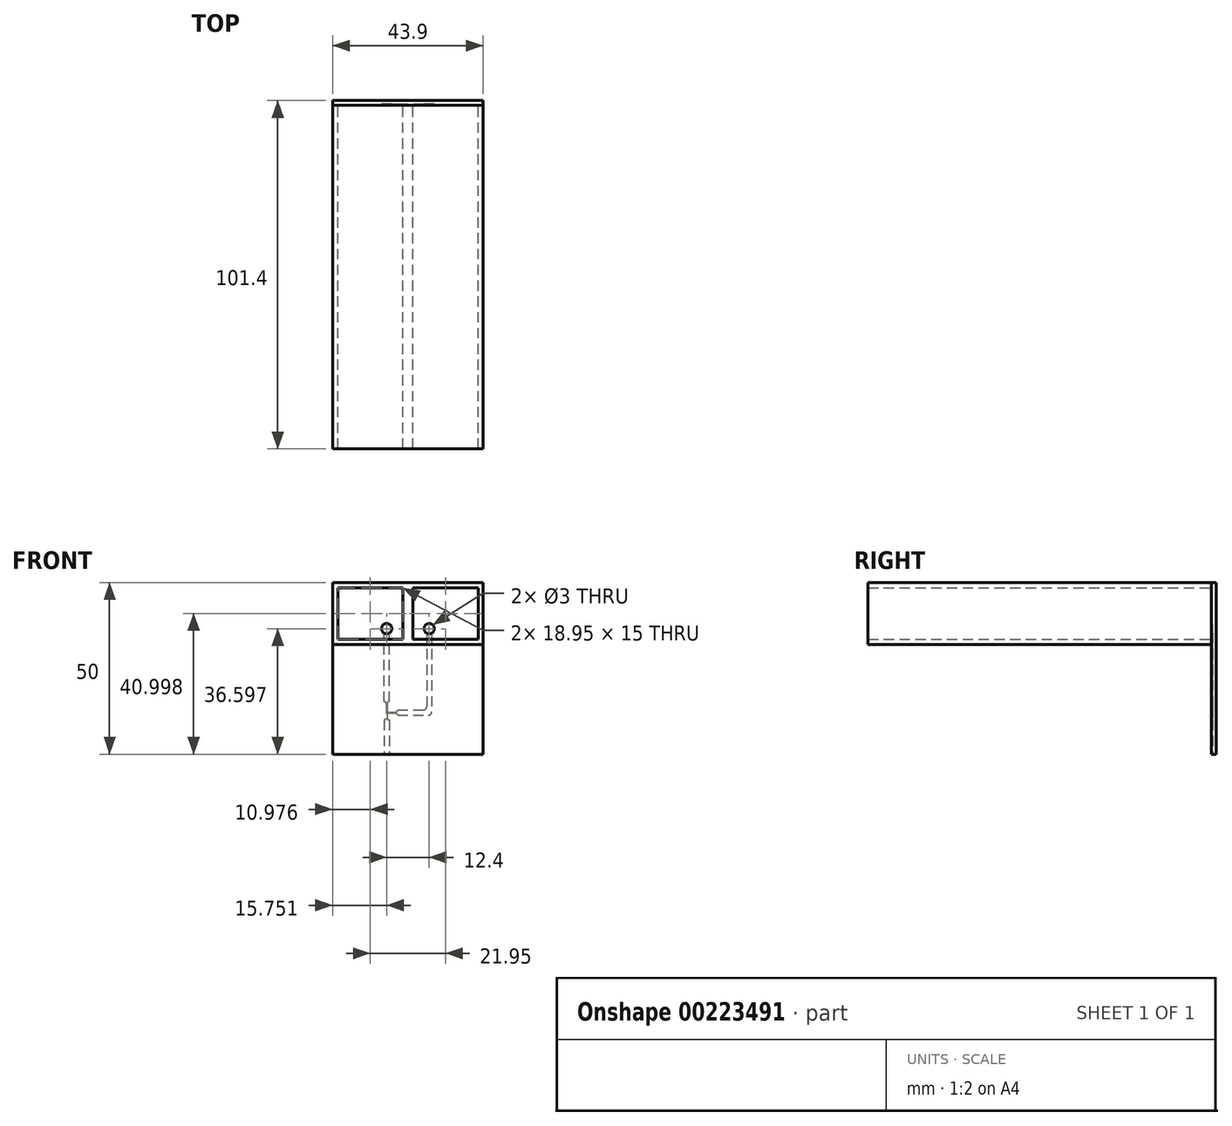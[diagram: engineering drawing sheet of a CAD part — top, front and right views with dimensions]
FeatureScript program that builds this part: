
annotation { "Feature Type Name" : "Feature", "Feature Type Description" : "" }
export const myFeature = defineFeature(function(context is Context, id is Id, definition is map)
    precondition{}
    {
        {
            var Q0;
            Q0=qCreatedBy(makeId("Front.planeOp"),FACE);
            var sketch = newSketch(context, id + "F0", { "sketchPlane" : qUnion([Q0])});
            skLineSegment(sketch, "E0.top", {"start": v(-31.06, -25.74) * mm, "end": v(-30.76, -25.74) * mm, "construction": true});
            skLineSegment(sketch, "E0.left", {"start": v(-31.06, -20.94) * mm, "end": v(-31.06, -25.24) * mm});
            skLineSegment(sketch, "E0.right", {"start": v(-30.76, -20.94) * mm, "end": v(-30.76, -23.44) * mm});
            skLineSegment(sketch, "E1.bottom", {"start": v(-30.76, -23.44) * mm, "end": v(-28.26, -23.44) * mm});
            skLineSegment(sketch, "E1.top", {"start": v(-30.76, -23.74) * mm, "end": v(-28.26, -23.74) * mm});
            skLineSegment(sketch, "E2.trimOffspring", {"start": v(-30.76, -23.74) * mm, "end": v(-30.76, -25.24) * mm});
            skLineSegment(sketch, "E3.bottom", {"start": v(-30.16, -25.74) * mm, "end": v(-30.26, -25.74) * mm});
            skLineSegment(sketch, "E3.left", {"start": v(-30.16, -25.74) * mm, "end": v(-30.16, -35.74) * mm});
            skLineSegment(sketch, "E3.right", {"start": v(-31.66, -25.74) * mm, "end": v(-31.66, -35.74) * mm});
            skPoint(sketch, "E3.middle", {"position": v(-30.9, -30.74) * mm});
            skPoint(sketch, "E3.middle.positionSnap0", {"position": v(-30.9, -25.74) * mm});
            skPoint(sketch, "E3.centerSnap0", {"position": v(-30.9, -25.74) * mm});
            skLineSegment(sketch, "E4.bottom", {"start": v(-27.76, -22.84) * mm, "end": v(-20.26, -22.84) * mm});
            skLineSegment(sketch, "E4.top", {"start": v(-27.76, -24.34) * mm, "end": v(-18.76, -24.34) * mm});
            skLineSegment(sketch, "E4.left", {"start": v(-27.76, -22.84) * mm, "end": v(-27.76, -22.94) * mm});
            skPoint(sketch, "E4.middle", {"position": v(-22.76, -23.6) * mm});
            skPoint(sketch, "E4.middle.positionSnap0", {"position": v(-27.76, -23.6) * mm});
            skPoint(sketch, "E4.centerSnap0", {"position": v(-27.76, -23.6) * mm});
            skLineSegment(sketch, "E5.bottom", {"start": v(-30.16, -20.44) * mm, "end": v(-30.26, -20.44) * mm});
            skLineSegment(sketch, "E5.left", {"start": v(-30.16, -20.44) * mm, "end": v(-30.16, -0.44) * mm});
            skLineSegment(sketch, "E5.right", {"start": v(-31.66, -20.44) * mm, "end": v(-31.66, -0.44) * mm});
            skPoint(sketch, "E5.middle", {"position": v(-30.9, -10.44) * mm});
            skPoint(sketch, "E5.middle.positionSnap0", {"position": v(-30.9, -20.44) * mm});
            skPoint(sketch, "E5.cornerSnap0", {"position": v(-30.9, -20.44) * mm});
            skPoint(sketch, "E5.centerSnap0", {"position": v(-30.9, -20.44) * mm});
            skLineSegment(sketch, "E6.trimOffspring", {"start": v(-31.56, -25.74) * mm, "end": v(-31.66, -25.74) * mm});
            skArc(sketch, "E7.filletArc", {"start": v(-31.56, -25.74) * mm, "mid": v(-31.2, -25.6) * mm, "end": v(-31.06, -25.24) * mm});
            skPoint(sketch, "E8.visualSharp", {"position": v(-30.76, -25.74) * mm});
            skArc(sketch, "E8.filletArc", {"start": v(-30.76, -25.24) * mm, "mid": v(-30.61, -25.6) * mm, "end": v(-30.26, -25.74) * mm});
            skLineSegment(sketch, "E9.trimOffspring", {"start": v(-27.76, -24.24) * mm, "end": v(-27.76, -24.34) * mm});
            skPoint(sketch, "E10.visualSharp", {"position": v(-27.76, -23.44) * mm});
            skArc(sketch, "E10.filletArc", {"start": v(-28.26, -23.44) * mm, "mid": v(-27.9, -23.3) * mm, "end": v(-27.76, -22.94) * mm});
            skPoint(sketch, "E11.visualSharp", {"position": v(-27.76, -23.74) * mm});
            skArc(sketch, "E11.filletArc", {"start": v(-27.76, -24.24) * mm, "mid": v(-27.9, -23.89) * mm, "end": v(-28.26, -23.74) * mm});
            skLineSegment(sketch, "E12.trimOffspring", {"start": v(-31.56, -20.44) * mm, "end": v(-31.66, -20.44) * mm});
            skPoint(sketch, "E13.visualSharp", {"position": v(-30.76, -20.44) * mm});
            skArc(sketch, "E13.filletArc", {"start": v(-30.26, -20.44) * mm, "mid": v(-30.61, -20.59) * mm, "end": v(-30.76, -20.94) * mm});
            skPoint(sketch, "E14.visualSharp", {"position": v(-31.06, -20.44) * mm});
            skArc(sketch, "E14.filletArc", {"start": v(-31.06, -20.94) * mm, "mid": v(-31.2, -20.59) * mm, "end": v(-31.56, -20.44) * mm});
            skArc(sketch, "E15", {"start": v(-30.16, -0.44) * mm, "mid": v(-30.9, 2.36) * mm, "end": v(-31.66, -0.44) * mm});
            skPoint(sketch, "E15.centerSnap0", {"position": v(-30.9, -0.44) * mm});
            skLineSegment(sketch, "E16.bottom", {"start": v(-46.66, -35.74) * mm, "end": v(-31.66, -35.74) * mm});
            skLineSegment(sketch, "E16.top", {"start": v(-46.66, 14.26) * mm, "end": v(-2.76, 14.26) * mm});
            skLineSegment(sketch, "E16.left", {"start": v(-46.66, -35.74) * mm, "end": v(-46.66, 14.26) * mm});
            skLineSegment(sketch, "E16.right", {"start": v(-2.76, -35.74) * mm, "end": v(-2.76, 14.26) * mm});
            skLineSegment(sketch, "E17.trimOffspring", {"start": v(-30.16, -35.74) * mm, "end": v(-2.76, -35.74) * mm});
            skLineSegment(sketch, "E18.left", {"start": v(-19.26, -0.44) * mm, "end": v(-19.26, -21.84) * mm});
            skLineSegment(sketch, "E18.right", {"start": v(-17.76, -0.44) * mm, "end": v(-17.76, -23.34) * mm});
            skPoint(sketch, "E19.visualSharp", {"position": v(-19.26, -22.84) * mm});
            skArc(sketch, "E19.filletArc", {"start": v(-20.26, -22.84) * mm, "mid": v(-19.55, -22.55) * mm, "end": v(-19.26, -21.84) * mm});
            skPoint(sketch, "E20.visualSharp", {"position": v(-17.76, -24.34) * mm});
            skArc(sketch, "E20.filletArc", {"start": v(-18.76, -24.34) * mm, "mid": v(-18.05, -24.05) * mm, "end": v(-17.76, -23.34) * mm});
            skLineSegment(sketch, "E21", {"start": v(-27.76, -23.6) * mm, "end": v(-22.76, -23.6) * mm, "construction": true});
            skLineSegment(sketch, "E22", {"start": v(-22.76, -23.6) * mm, "end": v(-22.76, -22.84) * mm, "construction": true});
            skArc(sketch, "E23", {"start": v(-17.76, -0.44) * mm, "mid": v(-18.5, 2.36) * mm, "end": v(-19.26, -0.44) * mm});
            skPoint(sketch, "E23.centerSnap0", {"position": v(-18.5, -0.44) * mm});
            skSolve(sketch);
        }
        {
            var Q0;
            Q0=makeQuery(id+"F0.imprint","IMPRINT",FACE,{"disambiguationData":[TD([[makeQuery(id+"F0.imprint","IMPRINT",EDGE,{"derivedFrom":sQuery(id+"F0.wireOp",EDGE,"E0.left")}),-1.0]])]});
            extrude(context, id + "F1", {"entities" : qUnion([Q0]), "depth" : .3 * mm});
        }
        {
            var Q0;
            Q0=makeQuery(id+"F1.opExtrude","CAP_FACE",FACE,{"disambiguationData":[OSD([sQuery(id+"F0.wireOp",EDGE,"E0.left"),sQuery(id+"F0.wireOp",EDGE,"E0.right"),sQuery(id+"F0.wireOp",EDGE,"E1.bottom"),sQuery(id+"F0.wireOp",EDGE,"E1.top"),sQuery(id+"F0.wireOp",EDGE,"E2.trimOffspring"),sQuery(id+"F0.wireOp",EDGE,"E3.bottom"),sQuery(id+"F0.wireOp",EDGE,"E3.left"),sQuery(id+"F0.wireOp",EDGE,"E3.right"),sQuery(id+"F0.wireOp",EDGE,"E4.bottom"),sQuery(id+"F0.wireOp",EDGE,"E4.top"),sQuery(id+"F0.wireOp",EDGE,"E4.left"),sQuery(id+"F0.wireOp",EDGE,"E5.bottom"),sQuery(id+"F0.wireOp",EDGE,"E5.left"),sQuery(id+"F0.wireOp",EDGE,"E5.right"),sQuery(id+"F0.wireOp",EDGE,"E6.trimOffspring"),sQuery(id+"F0.wireOp",EDGE,"E7.filletArc"),sQuery(id+"F0.wireOp",EDGE,"E8.filletArc"),sQuery(id+"F0.wireOp",EDGE,"E9.trimOffspring"),sQuery(id+"F0.wireOp",EDGE,"E10.filletArc"),sQuery(id+"F0.wireOp",EDGE,"E11.filletArc"),sQuery(id+"F0.wireOp",EDGE,"E12.trimOffspring"),sQuery(id+"F0.wireOp",EDGE,"E13.filletArc"),sQuery(id+"F0.wireOp",EDGE,"E14.filletArc"),sQuery(id+"F0.wireOp",EDGE,"sbfGVLC7-NtCD-0sHw-2H6X-rHgn86cjMGdF"),sQuery(id+"F0.wireOp",EDGE,"E15"),sQuery(id+"F0.wireOp",EDGE,"E16.bottom"),sQuery(id+"F0.wireOp",EDGE,"E16.top"),sQuery(id+"F0.wireOp",EDGE,"E16.left"),sQuery(id+"F0.wireOp",EDGE,"E16.right"),sQuery(id+"F0.wireOp",EDGE,"E17.trimOffspring")])],"isStart":true});
            var sketch = newSketch(context, id + "F2", { "sketchPlane" : qUnion([Q0])});
            skLineSegment(sketch, "E24.bottom", {"start": v(46.66, -35.74) * mm, "end": v(2.76, -35.74) * mm});
            skLineSegment(sketch, "E24.top", {"start": v(46.66, 14.26) * mm, "end": v(2.76, 14.26) * mm});
            skLineSegment(sketch, "E24.left", {"start": v(46.66, -35.74) * mm, "end": v(46.66, 14.26) * mm});
            skLineSegment(sketch, "E24.right", {"start": v(2.76, -35.74) * mm, "end": v(2.76, 14.26) * mm});
            skSolve(sketch);
        }
        {
            var Q0;
            Q0 = qSketchRegion(id + "F2", true);
            extrude(context, id + "F3", {"entities" : qUnion([Q0]), "operationType" : NewBodyOperationType.ADD, "depth" : 1 * mm});
        }
        {
            var Q0;
            Q0=makeQuery(id+"F1.opExtrude","CAP_FACE",FACE,{"disambiguationData":[OSD([sQuery(id+"F0.wireOp",EDGE,"E0.left"),sQuery(id+"F0.wireOp",EDGE,"E0.right"),sQuery(id+"F0.wireOp",EDGE,"E1.bottom"),sQuery(id+"F0.wireOp",EDGE,"E1.top"),sQuery(id+"F0.wireOp",EDGE,"E2.trimOffspring"),sQuery(id+"F0.wireOp",EDGE,"E3.bottom"),sQuery(id+"F0.wireOp",EDGE,"E3.left"),sQuery(id+"F0.wireOp",EDGE,"E3.right"),sQuery(id+"F0.wireOp",EDGE,"E4.bottom"),sQuery(id+"F0.wireOp",EDGE,"E4.top"),sQuery(id+"F0.wireOp",EDGE,"E4.left"),sQuery(id+"F0.wireOp",EDGE,"E5.bottom"),sQuery(id+"F0.wireOp",EDGE,"E5.left"),sQuery(id+"F0.wireOp",EDGE,"E5.right"),sQuery(id+"F0.wireOp",EDGE,"E6.trimOffspring"),sQuery(id+"F0.wireOp",EDGE,"E7.filletArc"),sQuery(id+"F0.wireOp",EDGE,"E8.filletArc"),sQuery(id+"F0.wireOp",EDGE,"E9.trimOffspring"),sQuery(id+"F0.wireOp",EDGE,"E10.filletArc"),sQuery(id+"F0.wireOp",EDGE,"E11.filletArc"),sQuery(id+"F0.wireOp",EDGE,"E12.trimOffspring"),sQuery(id+"F0.wireOp",EDGE,"E13.filletArc"),sQuery(id+"F0.wireOp",EDGE,"E14.filletArc"),sQuery(id+"F0.wireOp",EDGE,"E15"),sQuery(id+"F0.wireOp",EDGE,"E16.bottom"),sQuery(id+"F0.wireOp",EDGE,"E16.top"),sQuery(id+"F0.wireOp",EDGE,"E16.left"),sQuery(id+"F0.wireOp",EDGE,"E16.right"),sQuery(id+"F0.wireOp",EDGE,"E17.trimOffspring"),sQuery(id+"F0.wireOp",EDGE,"E18.left"),sQuery(id+"F0.wireOp",EDGE,"E18.right"),sQuery(id+"F0.wireOp",EDGE,"E19.filletArc"),sQuery(id+"F0.wireOp",EDGE,"E20.filletArc"),sQuery(id+"F0.wireOp",EDGE,"E23")])],"isStart":false});
            var sketch = newSketch(context, id + "F4", { "sketchPlane" : qUnion([Q0])});
            skLineSegment(sketch, "E25.bottom", {"start": v(-46.66, 14.26) * mm, "end": v(-2.76, 14.26) * mm});
            skLineSegment(sketch, "E25.top", {"start": v(-46.66, -35.74) * mm, "end": v(-2.76, -35.74) * mm});
            skLineSegment(sketch, "E25.left", {"start": v(-46.66, 14.26) * mm, "end": v(-46.66, -35.74) * mm});
            skLineSegment(sketch, "E25.right", {"start": v(-2.76, 14.26) * mm, "end": v(-2.76, -35.74) * mm});
            skArc(sketch, "E26.0", {"start": v(-30.16, -0.44) * mm, "mid": v(-30.9, 2.36) * mm, "end": v(-31.66, -0.44) * mm, "construction": true});
            skArc(sketch, "E26.1", {"start": v(-17.76, -0.44) * mm, "mid": v(-18.5, 2.36) * mm, "end": v(-19.26, -0.44) * mm, "construction": true});
            skCircle(sketch, "E27", {"center": v(-30.9, 0.86) * mm, "radius": 1.5 * mm});
            skCircle(sketch, "E28", {"center": v(-18.5, 0.86) * mm, "radius": 1.5 * mm});
            skSolve(sketch);
        }
        {
            var Q0;
            Q0 = qSketchRegion(id + "F4", true);
            extrude(context, id + "F5", {"entities" : qUnion([Q0]), "depth" : .1 * mm});
        }
        {
            var Q0;
            Q0=makeQuery(id+"F5.opExtrude","CAP_FACE",FACE,{"disambiguationData":[OSD([sQuery(id+"F4.wireOp",EDGE,"E25.bottom"),sQuery(id+"F4.wireOp",EDGE,"E25.top"),sQuery(id+"F4.wireOp",EDGE,"E25.left"),sQuery(id+"F4.wireOp",EDGE,"E25.right")])],"isStart":false});
            var sketch = newSketch(context, id + "F6", { "sketchPlane" : qUnion([Q0])});
            skPoint(sketch, "E29.firstSnap0", {"position": v(-24.7, 14.26) * mm});
            skLineSegment(sketch, "E29.bottom", {"start": v(-24.7, -3.74) * mm, "end": v(-46.66, -3.74) * mm});
            skLineSegment(sketch, "E29.top", {"start": v(-24.7, 14.26) * mm, "end": v(-46.66, 14.26) * mm});
            skLineSegment(sketch, "E29.right", {"start": v(-46.66, -3.74) * mm, "end": v(-46.66, 14.26) * mm});
            skLineSegment(sketch, "E30.bottom", {"start": v(-24.7, -3.74) * mm, "end": v(-2.76, -3.74) * mm});
            skLineSegment(sketch, "E30.top", {"start": v(-24.7, 14.26) * mm, "end": v(-2.76, 14.26) * mm});
            skLineSegment(sketch, "E30.right", {"start": v(-2.76, -3.74) * mm, "end": v(-2.76, 14.26) * mm});
            skLineSegment(sketch, "E31.bottom", {"start": v(-26.2, 12.76) * mm, "end": v(-45.16, 12.76) * mm});
            skLineSegment(sketch, "E31.top", {"start": v(-26.2, -2.24) * mm, "end": v(-45.16, -2.24) * mm});
            skLineSegment(sketch, "E31.left", {"start": v(-26.2, 12.76) * mm, "end": v(-26.2, -2.24) * mm});
            skLineSegment(sketch, "E31.right", {"start": v(-45.16, 12.76) * mm, "end": v(-45.16, -2.24) * mm});
            skPoint(sketch, "E31.middle", {"position": v(-35.68, 5.26) * mm});
            skPoint(sketch, "E31.middle.positionSnap0", {"position": v(-24.7, 5.26) * mm});
            skPoint(sketch, "E31.middle.positionSnap1", {"position": v(-35.68, 14.26) * mm});
            skPoint(sketch, "E31.centerSnap0", {"position": v(-24.7, 5.26) * mm});
            skPoint(sketch, "E31.centerSnap1", {"position": v(-35.68, 14.26) * mm});
            skLineSegment(sketch, "E32.MirrorCS", {"start": v(-23.2, 12.76) * mm, "end": v(-23.2, -2.24) * mm});
            skLineSegment(sketch, "E33.MirrorCS", {"start": v(-23.2, -2.24) * mm, "end": v(-4.26, -2.24) * mm});
            skLineSegment(sketch, "E34.MirrorCS", {"start": v(-4.26, 12.76) * mm, "end": v(-4.26, -2.24) * mm});
            skLineSegment(sketch, "E35.MirrorCS", {"start": v(-23.2, 12.76) * mm, "end": v(-4.26, 12.76) * mm});
            skSolve(sketch);
        }
        {
            var Q0;
            Q0=makeQuery(id+"F6.imprint","IMPRINT",FACE,{"disambiguationData":[TD([[makeQuery(id+"F6.imprint","IMPRINT",EDGE,{"derivedFrom":sQuery(id+"F6.wireOp",EDGE,"E29.bottom")}),-1.0]])]});
            extrude(context, id + "F7", {"entities" : qUnion([Q0]), "depth" : 100 * mm});
        }
    });
